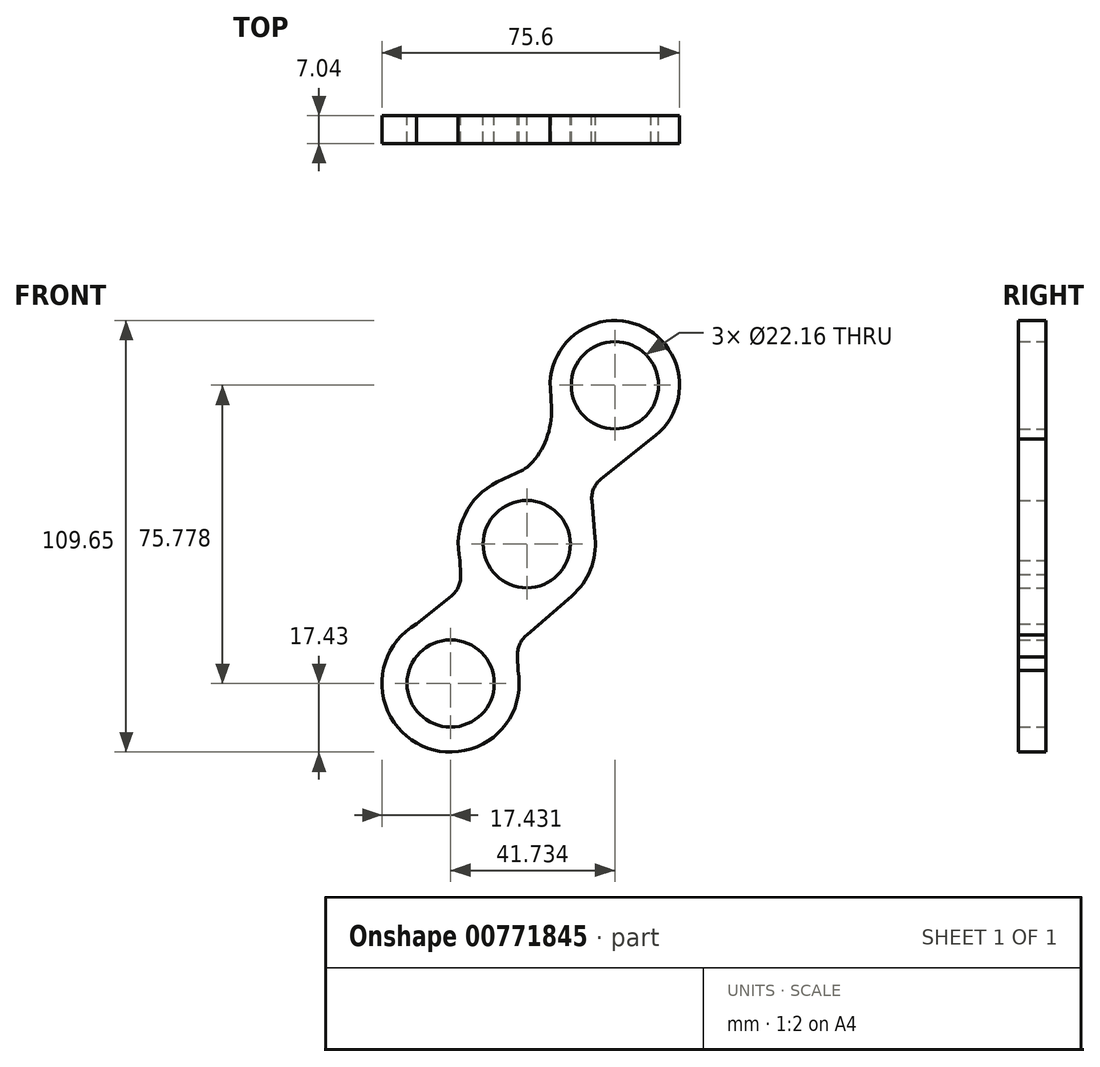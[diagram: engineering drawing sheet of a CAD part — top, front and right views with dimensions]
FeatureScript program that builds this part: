
annotation { "Feature Type Name" : "Feature", "Feature Type Description" : "" }
export const myFeature = defineFeature(function(context is Context, id is Id, definition is map)
    precondition{}
    {
        {
            var Q0;
            Q0=qCreatedBy(makeId("Front.planeOp"),FACE);
            var sketch = newSketch(context, id + "F0", { "sketchPlane" : qUnion([Q0])});
            skCircle(sketch, "E0", {"center": v(-40.25, 35.42) * mm, "radius": 11.08 * mm});
            skCircle(sketch, "E1", {"center": v(-40.25, 35.42) * mm, "radius": 17.43 * mm});
            skCircle(sketch, "E2", {"center": v(-17.88, 75.78) * mm, "radius": 11.08 * mm});
            skLineSegment(sketch, "E3", {"start": v(-47.78, 51.14) * mm, "end": v(-41.26, 54.3) * mm});
            skArc(sketch, "E4.filletArc", {"start": v(-41.26, 54.3) * mm, "mid": v(-40.33, 54.85) * mm, "end": v(-39.51, 55.55) * mm});
            skLineSegment(sketch, "E5", {"start": v(-22.9, 36.97) * mm, "end": v(-23.74, 46.44) * mm});
            skCircle(sketch, "E6", {"center": v(-17.88, 75.78) * mm, "radius": 16.44 * mm});
            skLineSegment(sketch, "E7", {"start": v(-34.04, 69.9) * mm, "end": v(-34.3, 74.94) * mm});
            skLineSegment(sketch, "E8", {"start": v(-6.53, 63.88) * mm, "end": v(-21.39, 51.96) * mm});
            skArc(sketch, "E9.filletArc", {"start": v(-39.51, 55.55) * mm, "mid": v(-35.26, 62.15) * mm, "end": v(-34.04, 69.9) * mm});
            skPoint(sketch, "E10.visualSharp", {"position": v(-24.04, 49.83) * mm});
            skArc(sketch, "E10.filletArc", {"start": v(-21.39, 51.96) * mm, "mid": v(-23.26, 49.5) * mm, "end": v(-23.74, 46.44) * mm});
            skCircle(sketch, "E11", {"center": v(-59.6, 0) * mm, "radius": 11.08 * mm});
            skCircle(sketch, "E12", {"center": v(-59.6, 0) * mm, "radius": 17.43 * mm});
            skLineSegment(sketch, "E13", {"start": v(-74.29, 10.31) * mm, "end": v(-59.43, 22.23) * mm});
            skArc(sketch, "E14.filletArc", {"start": v(-59.43, 22.23) * mm, "mid": v(-57.56, 24.7) * mm, "end": v(-57.08, 27.75) * mm});
            skLineSegment(sketch, "E15", {"start": v(-57.08, 27.75) * mm, "end": v(-57.18, 31.27) * mm});
            skArc(sketch, "E16.filletArc", {"start": v(-40.25, 12.31) * mm, "mid": v(-42.11, 9.85) * mm, "end": v(-42.6, 6.8) * mm});
            skLineSegment(sketch, "E17", {"start": v(-42.6, 6.8) * mm, "end": v(-42.5, 3.28) * mm});
            skLineSegment(sketch, "E18", {"start": v(-40.25, 12.31) * mm, "end": v(-28.8, 22.27) * mm});
            skSolve(sketch);
        }
        {
            var Q0;
            Q0 = qSketchRegion(id + "F0", true);
            extrude(context, id + "F1", {"entities" : qUnion([Q0]), "depth" : 7.04 * mm, "offsetDistance" : 25.4 * mm});
        }
    });
